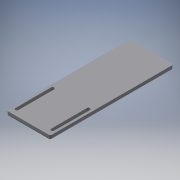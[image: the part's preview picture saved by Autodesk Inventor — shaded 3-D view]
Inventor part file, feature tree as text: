
AUTODESK INVENTOR PART (.ipt)
format: ipt  version: 2018 (Build 220112000, 112)  size: 145,920 bytes
history: native  units: mm
features: other x4, extrude x3, sketch x3, fillet x2, reference x2, projected_geometry x1
ambient origin geometry x8: Origin, YZ Plane, XZ Plane, XY Plane, X Axis, Y Axis, Z Axis, Center Point
bodies: Solid1 (feature_tree)
feature tree (15):
  extrude  "Extrusion1"  Depth=55.0mm
  extrude  "Extrusion2"  Depth=5.5mm TaperAngle=0.0deg
  extrude  "Extrusion3"  Depth=4.0mm
  fillet  "Fillet1"  Radius=45.0mm
  fillet  "Fillet2"  Radius=4.0mm
  sketch  "Sketch1"  dims[d0=125.0mm d1=55.0mm]
  reference  "Reference1"
  sketch  "Sketch3"  dims[d2=5.5mm d3=0.0mm d4=30.0mm d5=0.0mm]
  projected_geometry  "Projected Loop1"
  sketch  "Sketch4"  dims[d6=4.0mm d7=4.0mm d8=45.0mm d9=4.0mm d10=45.0mm d11=4.0mm d12=30.0mm d13=0.0mm d14=2.0mm d15=2.0mm]
  reference  "Reference6"
  other  "<userpath>\OneDrive\Documents\Inventor\TSA\2018\Animatronics\Tortoise\Head\HeadAssembly.iam"
  other  "HeadAssembly.iam"
  other  "HeadRack:1"
  other  "HeadBottom:1"
